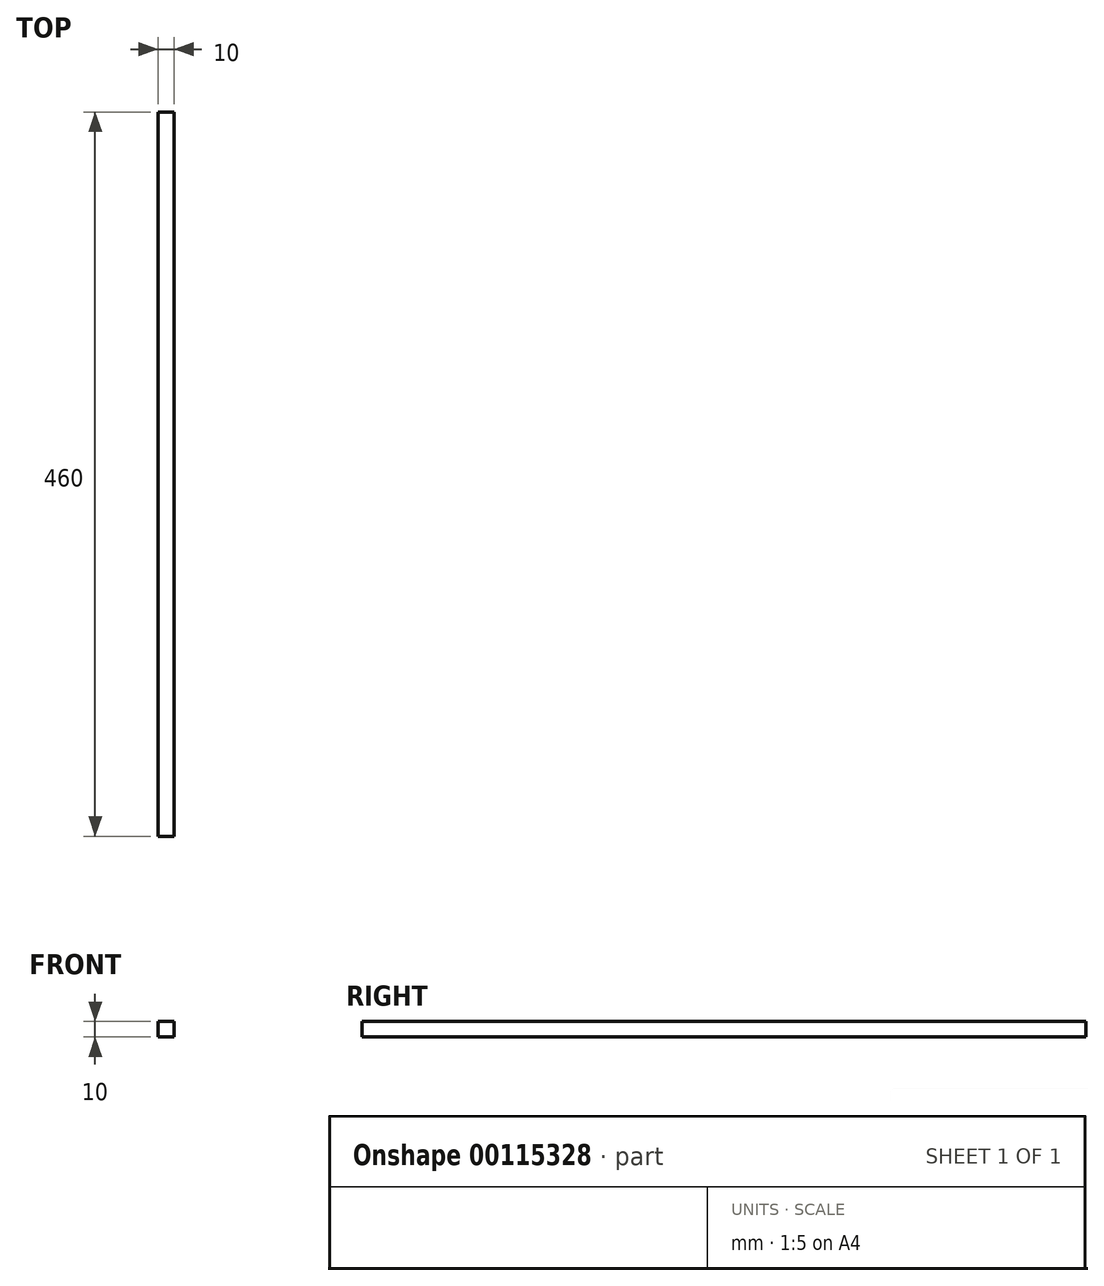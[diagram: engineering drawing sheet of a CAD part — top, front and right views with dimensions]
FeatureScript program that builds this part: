
annotation { "Feature Type Name" : "Feature", "Feature Type Description" : "" }
export const myFeature = defineFeature(function(context is Context, id is Id, definition is map)
    precondition{}
    {
        {
            var Q0;
            Q0=qCreatedBy(makeId("Top.planeOp"),FACE);
            var sketch = newSketch(context, id + "F0", { "sketchPlane" : qUnion([Q0])});
            skLineSegment(sketch, "E0.bottom", {"start": v(0, 0) * mm, "end": v(10, 0) * mm});
            skLineSegment(sketch, "E0.top", {"start": v(0, 460) * mm, "end": v(10, 460) * mm});
            skLineSegment(sketch, "E0.left", {"start": v(0, 0) * mm, "end": v(0, 460) * mm});
            skLineSegment(sketch, "E0.right", {"start": v(10, 0) * mm, "end": v(10, 460) * mm});
            skSolve(sketch);
        }
        {
            var Q0;
            Q0 = qSketchRegion(id + "F0", true);
            extrude(context, id + "F1", {"entities" : qUnion([Q0]), "depth" : 10 * mm});
        }
    });
